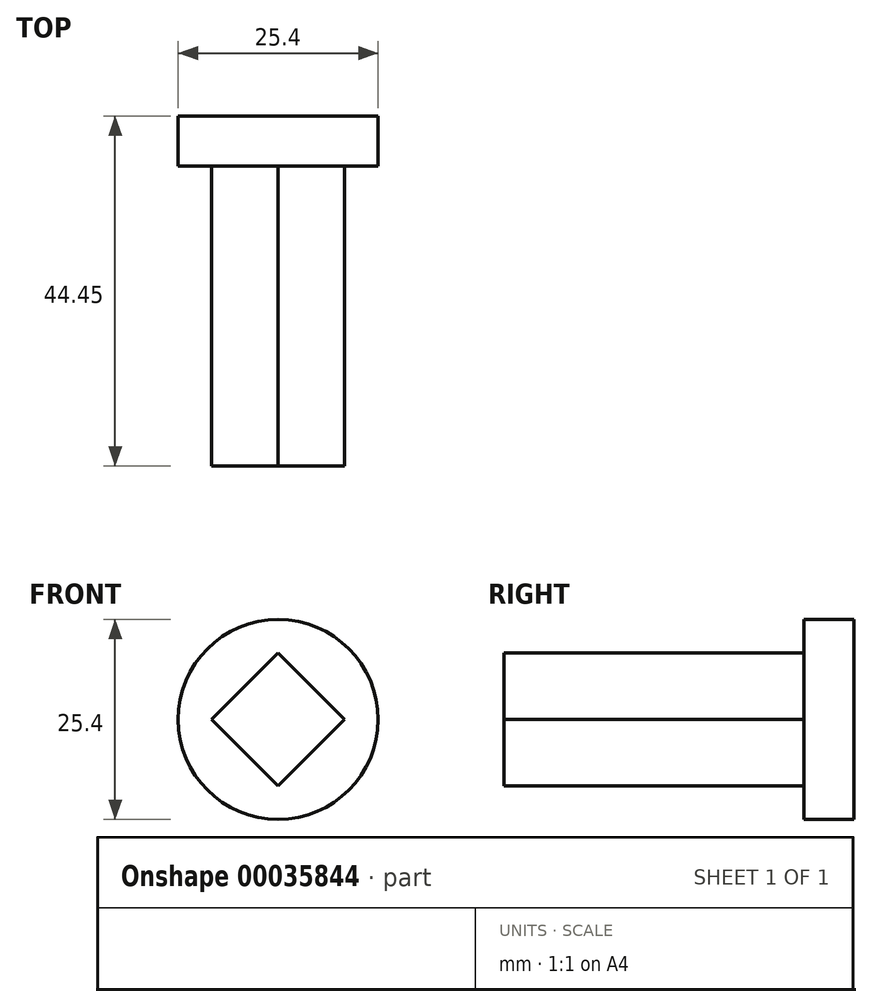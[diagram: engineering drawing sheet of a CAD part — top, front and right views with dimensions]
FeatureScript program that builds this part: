
annotation { "Feature Type Name" : "Feature", "Feature Type Description" : "" }
export const myFeature = defineFeature(function(context is Context, id is Id, definition is map)
    precondition{}
    {
        {
            var Q0;
            Q0=qCreatedBy(makeId("Front.planeOp"),FACE);
            var sketch = newSketch(context, id + "F0", { "sketchPlane" : qUnion([Q0])});
            skCircle(sketch, "E0", {"center": v(0, 0) * mm, "radius": 12.7 * mm});
            skSolve(sketch);
        }
        {
            var Q0;
            Q0=makeQuery(id+"F0.imprint","IMPRINT",FACE,{"disambiguationData":[TD([[makeQuery(id+"F0.imprint","IMPRINT",EDGE,{"derivedFrom":sQuery(id+"F0.wireOp",EDGE,"E0")}),1.0]])]});
            extrude(context, id + "F1", {"entities" : qUnion([Q0]), "depth" : 6.35 * mm});
        }
        {
            var Q0;
            Q0=makeQuery(id+"F1.opExtrude","CAP_FACE",FACE,{"disambiguationData":[OSD([sQuery(id+"F0.wireOp",EDGE,"E0")])],"isStart":false});
            var sketch = newSketch(context, id + "F2", { "sketchPlane" : qUnion([Q0])});
            skLineSegment(sketch, "E1.rect.bottom", {"start": v(8.44, 0) * mm, "end": v(0, -8.44) * mm});
            skLineSegment(sketch, "E1.rect.top", {"start": v(0, 8.44) * mm, "end": v(-8.44, 0) * mm});
            skLineSegment(sketch, "E1.rect.left", {"start": v(8.44, 0) * mm, "end": v(0, 8.44) * mm});
            skLineSegment(sketch, "E1.rect.right", {"start": v(0, -8.44) * mm, "end": v(-8.44, 0) * mm});
            skPoint(sketch, "E1.rect.middle", {"position": v(0, 0) * mm});
            skLineSegment(sketch, "E2", {"start": v(0, 32.53) * mm, "end": v(0, -35.6) * mm, "construction": true});
            skSolve(sketch);
        }
        {
            var Q0;
            Q0 = qSketchRegion(id + "F2", true);
            extrude(context, id + "F3", {"entities" : qUnion([Q0]), "operationType" : NewBodyOperationType.ADD, "depth" : 38.1 * mm});
        }
    });
